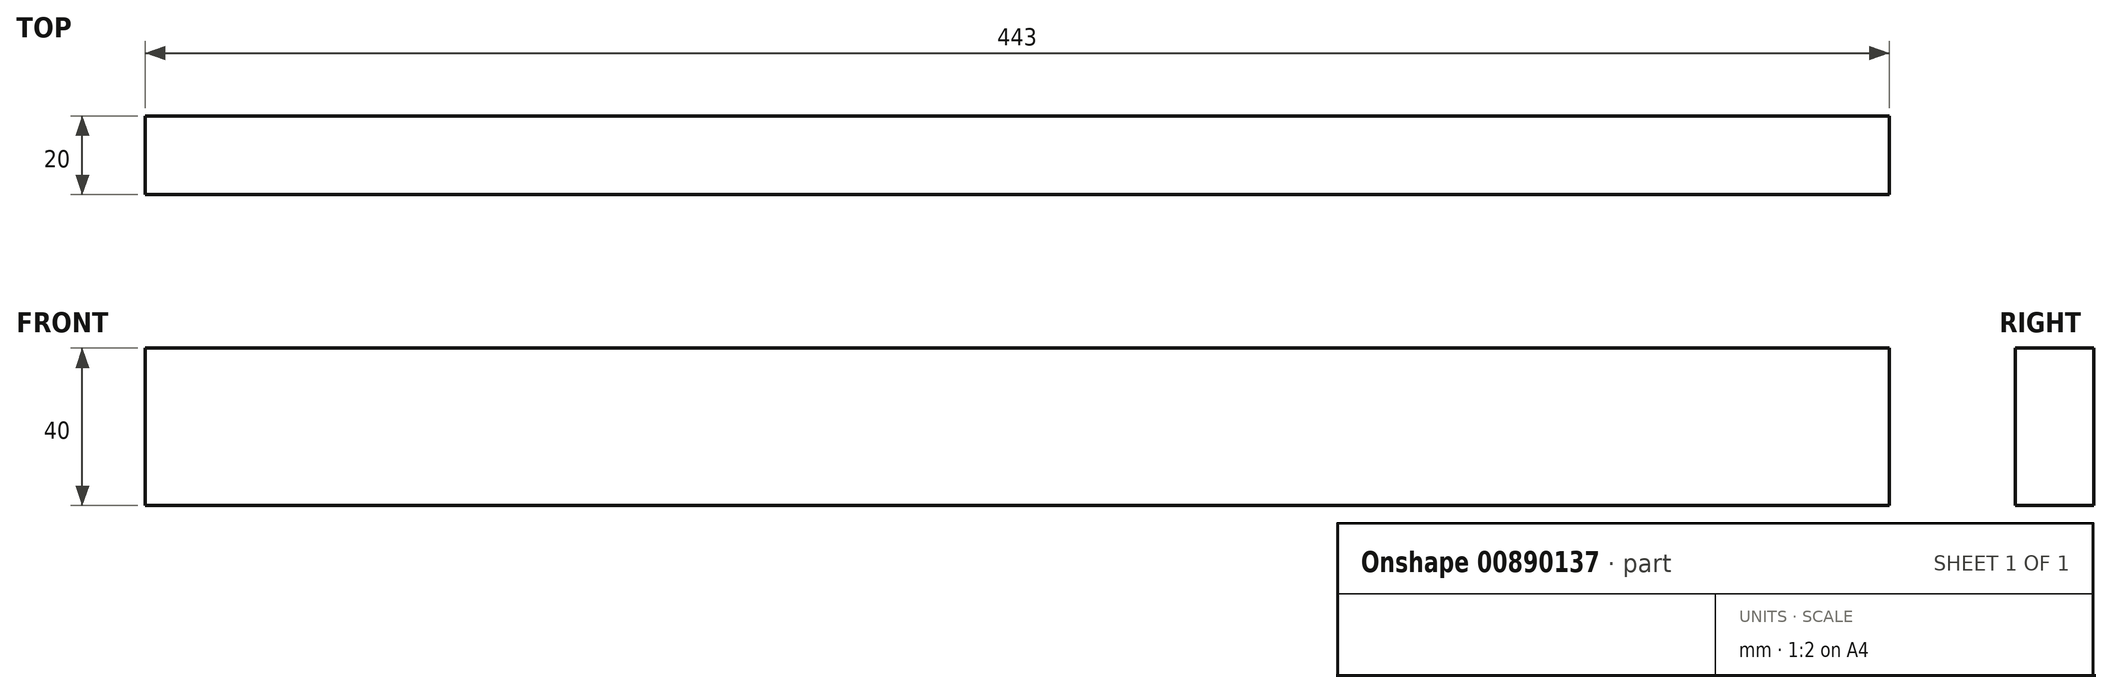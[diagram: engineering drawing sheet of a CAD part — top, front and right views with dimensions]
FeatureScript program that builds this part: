
annotation { "Feature Type Name" : "Feature", "Feature Type Description" : "" }
export const myFeature = defineFeature(function(context is Context, id is Id, definition is map)
    precondition{}
    {
        {
            var Q0;
            Q0=qCreatedBy(makeId("Front.planeOp"),FACE);
            var sketch = newSketch(context, id + "F0", { "sketchPlane" : qUnion([Q0])});
            skLineSegment(sketch, "E0.bottom", {"start": v(-221.5, 20) * mm, "end": v(221.5, 20) * mm});
            skLineSegment(sketch, "E0.top", {"start": v(-221.5, -20) * mm, "end": v(221.5, -20) * mm});
            skLineSegment(sketch, "E0.left", {"start": v(-221.5, 20) * mm, "end": v(-221.5, -20) * mm});
            skLineSegment(sketch, "E0.right", {"start": v(221.5, 20) * mm, "end": v(221.5, -20) * mm});
            skPoint(sketch, "E0.middle", {"position": v(0, 0) * mm});
            skPoint(sketch, "E1.centerSnap0", {"position": v(-221.5, 0) * mm});
            skPoint(sketch, "E2.centerSnap0", {"position": v(221.5, 0) * mm});
            skSolve(sketch);
        }
        {
            var Q0;
            Q0=qSketchRegion(id+"F0",true);
            extrude(context, id + "F1", {"entities" : qUnion([Q0]), "depth" : 20 * mm, "offsetDistance" : 25 * mm});
        }
    });
